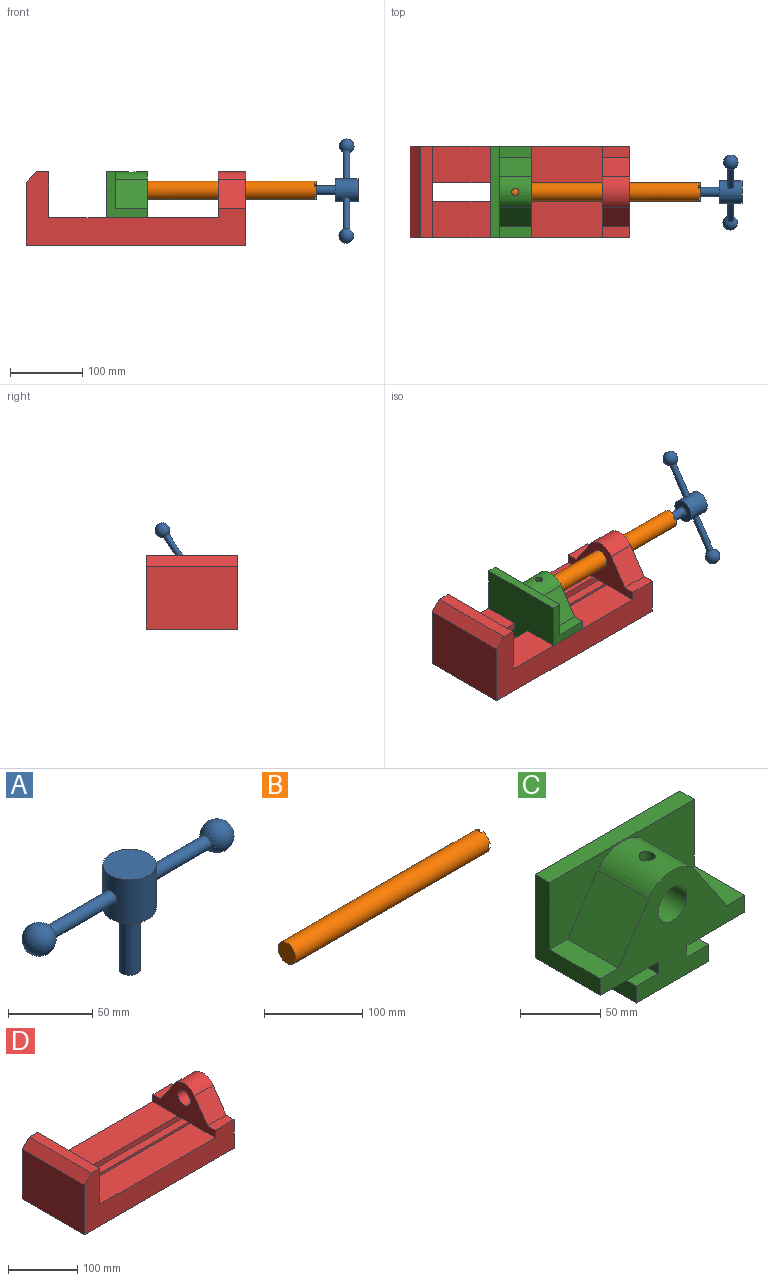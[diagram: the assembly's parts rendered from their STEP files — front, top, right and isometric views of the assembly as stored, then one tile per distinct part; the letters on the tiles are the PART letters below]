
ASSEMBLY  parts=4 mates=3
PART A: 9 faces, bbox 169.9x31.8x76.2 mm
  f0: cylinder r=4.45mm len=49.13mm, axis (-1,0,0), area 1361mm2, adj f1,f7
  f1: cylinder r=15.88mm len=31.75mm, axis (0,0,1), area 3041.5mm2, adj f0,f2,f3,f6
  f2: plane 31.75x31.75mm, normal (0,0,-1), area 665.1mm2, adj f1,f4
  f3: plane 31.75x31.75mm, normal (0,0,1), area 791.7mm2, adj f1
  f4: cylinder r=6.35mm len=44.45mm, axis (0,0,1), area 1773.5mm2, adj f2,f5
  f5: plane 12.7x12.7mm, normal (0,0,-1), area 126.7mm2, adj f4
  f6: cylinder r=4.45mm len=52.04mm, axis (-1,0,0), area 1438.7mm2, adj f1,f8
  f7: sphere r=10.16mm, area 1231.8mm2, adj f0
  f8: sphere r=10.16mm, area 1231.7mm2, adj f6
PART B: 20 faces, bbox 279.4x25.4x25.4 mm
  f0: plane 9.9x9.9mm, normal (1,0,0), area 62.3mm2, adj f3,f6,f15,f18
  f1: plane 9.9x9.9mm, normal (1,0,0), area 62.3mm2, adj f3,f13,f16,f18
  f2: plane 9.9x9.9mm, normal (1,0,0), area 62.3mm2, adj f3,f9,f12,f18
  f3: cylinder r=12.7mm len=279.4mm, axis (1,0,0), area 22243.2mm2, adj f0,f1,f2,f4,f5,f6,f7,f8
  f4: plane 9.9x9.9mm, normal (1,0,0), area 62.3mm2, adj f3,f7,f10,f18
  f5: plane 25.4x25.4mm, normal (-1,0,0), area 506.7mm2, adj f3
  f6: plane 6.62x2.54mm, normal (0,0,-1), area 16.8mm2, adj f0,f3,f8,f18
  f7: plane 6.62x2.54mm, normal (0,0,1), area 16.8mm2, adj f3,f4,f8,f18
  f8: plane 6.88x5.08mm, normal (1,0,0), area 32.7mm2, adj f3,f6,f7,f18
  f9: plane 6.62x2.54mm, normal (0,1,0), area 16.8mm2, adj f2,f3,f11,f18
  f10: plane 6.62x2.54mm, normal (0,-1,0), area 16.8mm2, adj f3,f4,f11,f18
  f11: plane 6.88x5.08mm, normal (1,0,0), area 32.7mm2, adj f3,f9,f10,f18
  f12: plane 6.62x2.54mm, normal (0,0,1), area 16.8mm2, adj f2,f3,f14,f18
  f13: plane 6.62x2.54mm, normal (0,0,-1), area 16.8mm2, adj f1,f3,f14,f18
  f14: plane 6.88x5.08mm, normal (1,0,0), area 32.7mm2, adj f3,f12,f13,f18
  f15: plane 6.62x2.54mm, normal (0,-1,0), area 16.8mm2, adj f0,f3,f17,f18
  f16: plane 6.62x2.54mm, normal (0,1,0), area 16.8mm2, adj f1,f3,f17,f18
  f17: plane 6.88x5.08mm, normal (1,0,0), area 32.7mm2, adj f3,f15,f16,f18
  f18: cylinder r=6.35mm len=19.05mm, axis (1,0,0), area 707mm2, adj f0,f1,f2,f4,f6,f7,f8,f9
  f19: plane 12.7x12.7mm, normal (1,0,0), area 126.7mm2, adj f18
PART C: 23 faces, bbox 127x57.2x85.1 mm
  f0: cylinder r=25.4mm len=44.45mm, axis (0,1,0), area 2127.7mm2, adj f5,f6,f19,f20,f22
  f1: cylinder r=12.7mm len=44.45mm, axis (0,1,0), area 3464.4mm2, adj f5,f21,f22
  f2: plane 44.45x15.88mm, normal (0,0,1), area 705.6mm2, adj f5,f6,f8,f19
  f3: plane 63.5x57.15mm, normal (0,0,-1), area 3629mm2, adj f4,f5,f14,f15
  f4: plane 127x85.09mm, normal (0,1,0), area 9096.8mm2, adj f3,f7,f8,f9,f11,f12,f13,f14
  f5: plane 127x84.96mm, normal (0,-1,0), area 5180.8mm2, adj f0,f1,f2,f3,f7,f8,f10,f11
  f6: plane 127x50.8mm, normal (0,-1,0), area 3409.2mm2, adj f0,f2,f7,f8,f9,f10,f19,f20
  f7: plane 63.5x57.15mm, normal (1,0,0), area 1371mm2, adj f4,f5,f6,f9,f10,f11
  f8: plane 63.5x57.15mm, normal (-1,0,0), area 1371mm2, adj f2,f4,f5,f6,f9,f18
  f9: plane 127x12.7mm, normal (0,0,1), area 1612.9mm2, adj f4,f6,f7,f8
  f10: plane 44.45x15.88mm, normal (0,0,1), area 705.6mm2, adj f5,f6,f7,f20
  f11: plane 57.15x50.8mm, normal (0,0,-1), area 2903.2mm2, adj f4,f5,f7,f12
  f12: plane 57.15x8.89mm, normal (1,0,0), area 508.1mm2, adj f4,f5,f11,f13
  f13: plane 57.15x19.05mm, normal (0,0,1), area 1088.7mm2, adj f4,f5,f12,f14
  f14: plane 57.15x12.7mm, normal (1,0,0), area 725.8mm2, adj f3,f4,f5,f13
  f15: plane 57.15x12.7mm, normal (-1,0,0), area 725.8mm2, adj f3,f4,f5,f16
  f16: plane 57.15x19.05mm, normal (0,0,1), area 1088.7mm2, adj f4,f5,f15,f17
  f17: plane 57.15x8.89mm, normal (-1,0,0), area 508.1mm2, adj f4,f5,f16,f18
  f18: plane 57.15x50.8mm, normal (0,0,-1), area 2903.2mm2, adj f4,f5,f8,f17
  f19: plane 44.45x39.45mm, normal (-0.83,0,0.56), area 2113.8mm2, adj f0,f2,f5,f6
  f20: plane 44.45x39.45mm, normal (0.83,0,0.56), area 2113.8mm2, adj f0,f5,f6,f10
  f21: plane 25.4x25.4mm, normal (0,-1,0), area 506.7mm2, adj f1
  f22: cylinder r=5.08mm len=13.76mm, axis (0,0,-1), area 414mm2, adj f0,f1
PART D: 28 faces, bbox 304.8x127x101.6 mm
  f0: plane 234.95x50.8mm, normal (0,0,1), area 11935.5mm2, adj f2,f8,f11,f21
  f1: plane 38.1x15.88mm, normal (0,0,1), area 604.8mm2, adj f6,f8,f10,f16
  f2: plane 127x101.6mm, normal (1,0,0), area 9516.1mm2, adj f0,f3,f5,f9,f10,f11,f18,f19
  f3: plane 127x17.46mm, normal (0,0,1), area 2217.7mm2, adj f2,f10,f11,f12
  f4: plane 127x87.31mm, normal (-1,0,0), area 11088.7mm2, adj f5,f10,f11,f12
  f5: plane 304.8x127mm, normal (0,0,-1), area 31774.1mm2, adj f2,f4,f6,f10,f11,f26,f27
  f6: plane 127x101.6mm, normal (1,0,0), area 7544.8mm2, adj f1,f5,f7,f10,f11,f13,f14,f15
  f7: plane 38.1x15.88mm, normal (0,0,1), area 604.8mm2, adj f6,f8,f11,f13
  f8: plane 127x63.5mm, normal (-1,0,0), area 4157.7mm2, adj f0,f1,f7,f9,f10,f11,f13,f14
  f9: plane 234.95x50.8mm, normal (0,0,1), area 11935.5mm2, adj f2,f8,f10,f22
  f10: plane 304.8x101.6mm, normal (0,-1,0), area 14010.8mm2, adj f1,f2,f3,f4,f5,f6,f8,f9
  f11: plane 304.8x101.6mm, normal (0,1,0), area 14010.8mm2, adj f0,f2,f3,f4,f5,f6,f7,f8
  f12: plane 127x14.29mm, normal (-0.71,0,0.71), area 2566.1mm2, adj f3,f4,f10,f11
  f13: plane 39.55x38.1mm, normal (0,0.83,0.56), area 1814.5mm2, adj f6,f7,f8,f14
  f14: cylinder r=25.4mm len=42.19mm, axis (1,0,0), area 1896.6mm2, adj f6,f8,f13,f16
  f15: cylinder r=12.7mm len=38.1mm, axis (1,0,0), area 3040.2mm2, adj f6,f8
  f16: plane 39.55x38.1mm, normal (0,-0.83,0.56), area 1814.5mm2, adj f1,f6,f8,f14
  f17: plane 38.1x25.4mm, normal (0,0,-1), area 967.7mm2, adj f6,f8,f21,f22
  f18: plane 273.05x19.05mm, normal (0,0,1), area 5201.6mm2, adj f2,f6,f19,f27
  f19: plane 273.05x12.7mm, normal (0,-1,0), area 3467.7mm2, adj f2,f6,f18,f20
  f20: plane 273.05x19.05mm, normal (0,0,-1), area 5201.6mm2, adj f2,f6,f19,f21
  f21: plane 273.05x8.89mm, normal (0,-1,0), area 2427.4mm2, adj f0,f2,f6,f17,f20
  f22: plane 273.05x8.89mm, normal (0,1,0), area 2427.4mm2, adj f2,f6,f9,f17,f23
  f23: plane 273.05x19.05mm, normal (0,0,-1), area 5201.6mm2, adj f2,f6,f22,f24
  f24: plane 273.05x12.7mm, normal (0,1,0), area 3467.7mm2, adj f2,f6,f23,f25
  f25: plane 273.05x19.05mm, normal (0,0,1), area 5201.6mm2, adj f2,f6,f24,f26
  f26: plane 273.05x16.51mm, normal (0,1,0), area 4508.1mm2, adj f2,f5,f6,f25
  f27: plane 273.05x16.51mm, normal (0,-1,0), area 4508.1mm2, adj f2,f5,f6,f18
PLACE A rot(axis=(0.69,0.21,0.69),156.2deg) t=(155.87,57.09,74.41)mm
PLACE B rot(axis=(1,0,0),146.1deg) t=(98.72,57.09,74.41)mm
PLACE C rot(axis=(0,0,1),90deg) t=(-180.68,57.09,14.85)mm
PLACE D t=(0.33,57.09,-1.66)mm fixed
MATE revolute C.f0 <-> B.f3  axis (-1,0,0) through (-180.68,57.09,74.41)mm
MATE slider D.f2 <-> C.f4  axis (1,0,0) through (-272.72,-6.41,36.44)mm
MATE fastened B.f3 <-> A.f1  axis (1,0,0) through (79.67,57.09,74.41)mm
